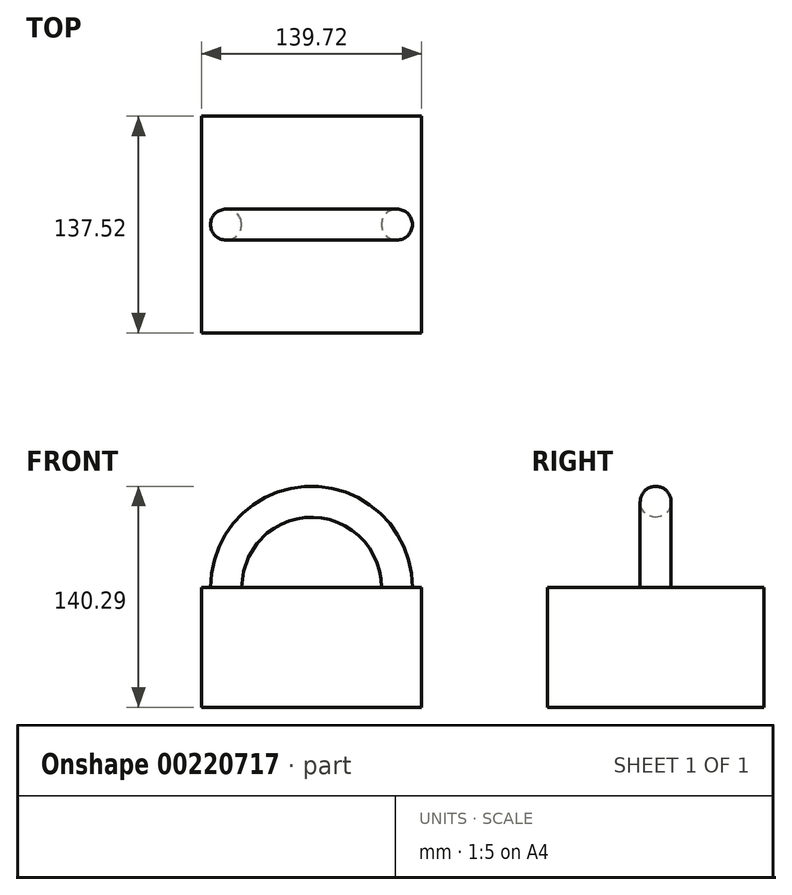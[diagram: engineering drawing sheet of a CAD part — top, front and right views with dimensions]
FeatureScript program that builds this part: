
annotation { "Feature Type Name" : "Feature", "Feature Type Description" : "" }
export const myFeature = defineFeature(function(context is Context, id is Id, definition is map)
    precondition{}
    {
        {
            var Q0;
            Q0=qCreatedBy(makeId("Top.planeOp"),FACE);
            var sketch = newSketch(context, id + "F0", { "sketchPlane" : qUnion([Q0])});
            skLineSegment(sketch, "E0.bottom", {"start": v(69.86, -68.76) * mm, "end": v(-69.86, -68.76) * mm});
            skLineSegment(sketch, "E0.top", {"start": v(69.86, 68.76) * mm, "end": v(-69.86, 68.76) * mm});
            skLineSegment(sketch, "E0.left", {"start": v(69.86, -68.76) * mm, "end": v(69.86, 68.76) * mm});
            skLineSegment(sketch, "E0.right", {"start": v(-69.86, -68.76) * mm, "end": v(-69.86, 68.76) * mm});
            skPoint(sketch, "E0.middle", {"position": v(0, 0) * mm});
            skLineSegment(sketch, "E1", {"start": v(0, 68.76) * mm, "end": v(0, -68.76) * mm});
            skSolve(sketch);
        }
        {
            var Q0;
            Q0=qCreatedBy(makeId("Top.planeOp"),FACE);
            var sketch = newSketch(context, id + "F1", { "sketchPlane" : qUnion([Q0])});
            skCircle(sketch, "E2", {"center": v(54.26, 0) * mm, "radius": 9.82 * mm});
            skSolve(sketch);
        }
        {
            var Q0;
            {var subQ0=sQuery(id+"F0.wireOp",EDGE,"E0.left");Q0=makeQuery(id+"F0.imprint","IMPRINT",FACE,{"disambiguationData":[TD([[makeQuery(id+"F0.imprint","IMPRINT",EDGE,{"derivedFrom":subQ0}),1.0]])]});}
            var Q1;
            {var subQ0=sQuery(id+"F0.wireOp",EDGE,"E0.right");Q1=makeQuery(id+"F0.imprint","IMPRINT",FACE,{"disambiguationData":[TD([[makeQuery(id+"F0.imprint","IMPRINT",EDGE,{"derivedFrom":subQ0}),-1.0]])]});}
            extrude(context, id + "F2", {"entities" : qUnion([Q0, Q1]), "oppositeDirection" : true, "depth" : 76.2 * mm});
        }
        {
            var Q0;
            Q0=makeQuery(id+"F1.imprint","IMPRINT",FACE,{"disambiguationData":[TD([[makeQuery(id+"F1.imprint","IMPRINT",EDGE,{"derivedFrom":sQuery(id+"F1.wireOp",EDGE,"E2")}),1.0]])]});
            var Q1;
            Q1=sQuery(id+"F0.wireOp",EDGE,"E1");
            revolve(context, id + "F3", {"operationType" : NewBodyOperationType.ADD, "entities" : qUnion([Q0]), "axis" : qUnion([Q1]), "revolveType" : RevolveType.FULL});
        }
    });
